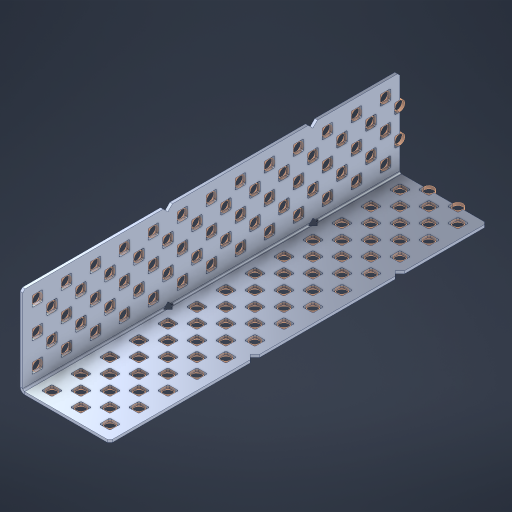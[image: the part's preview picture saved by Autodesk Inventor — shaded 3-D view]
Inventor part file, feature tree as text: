
AUTODESK INVENTOR PART (.ipt)
format: ipt  version: 2023 (Build 270158000, 158)  size: 1,572,352 bytes
history: native  units: in
note: dims shown in document units (in); Inventor stores cm internally (conversion verified against a paired STEP export)
features: other x136, extrude x128, sheet_metal_op x8, sketch x7, pattern_linear x3, mirror x1, chamfer x1
ambient origin geometry x8: Origin, YZ Plane, XZ Plane, XY Plane, X Axis, Y Axis, Z Axis, Center Point
bodies: Solid1 (feature_tree), Body (feature_tree)
feature tree (284):
  sheet_metal_op  "Flanges"
  sheet_metal_op  "Body Pattern"
  pattern_linear  "Center Double"  Spacing1=1.5in  [1 undecoded]
  pattern_linear  "Center Pattern"  Spacing1=0.1875in  [1 undecoded]
  other  "Arc Length"
  pattern_linear  "Notch Pattern"  Spacing1=0.0469in  [1 undecoded]
  other  "Diagonal Plane"
  mirror  "Everything Mirrored"
  chamfer  "End Chamfer"
  sketch  "Sketch1"  dims[d0=1.5in]
  other  "Plate1"
  sketch  "Sketch2"  dims[d1=6.5in]
  other  "Plate2"
  sheet_metal_op  "Bend1"
  sheet_metal_op  "Corner1"
  sketch  "Sketch8"  dims[d2=0.0469in]
  sketch  "Sketch9"  dims[d3=0.0469in]
  other  "Srf91"
  sheet_metal_op  "Body Pattern Sketch"
  other  "Srf92"
  sketch  "Sketch13"  dims[d4=0.0234in]
  sketch  "Sketch15"  dims[d5=0.0938in]
  sketch  "Sketch16"  dims[d6=0.0469in d7=1.5in d8=90.0deg d9=0.0312in d10=0.1875in d11=0.0469in d12=0.0469in d49=0.182in d50=0.02in d52=0.25in d53=0.0469in d54=0.0in d55=0.172in d56=1.0in d57=0.0in d85=0.1473in d86=0.1659in d89=0.0469in d90=0.0in d91=0.04in d92=0.0491in d95=2.5in d96=0.04in d97=0.25in d98=45.0deg d106=0.182in d107=0.02in d110=0.0469in d111=0.0in d112=0.172in d113=0.5in d114=0.0in d117=0.5in d126=0.0491in d127=0.1227in d128=0.08in d129=0.04in d130=2.5in d131=0.25in d132=5.1181in d134=0.5in d135=1.1811in d137=0.5in d140=0.5in d141=1.0in d142=0.3937in d144=0.5in d145=0.071in d146=0.7874in d148=0.5in]
  other  "Srf786"
  other  "Srf856"
  other  "Srf889"
  other  "Srf890"
  other  "Srf891"
  other  "Srf1275"
  other  "Srf1276"
  other  "Srf1278"
  other  "Srf1277"
  other  "Srf1285"
  other  "Srf1286"
  other  "Srf1287"
  other  "Srf1445"
  other  "Srf1446"
  other  "Srf1447"
  other  "Srf1448"
  other  "Srf1449"
  other  "Srf1537"
  other  "Srf1538"
  other  "Srf1539"
  other  "Srf1540"
  other  "Srf1541"
  other  "Srf1807"
  other  "Srf1808"
  other  "Srf1809"
  other  "Srf1810"
  other  "Srf1959"
  other  "Srf1960"
  other  "Srf1961"
  other  "Srf1962"
  other  "Srf2009"
  other  "Srf2010"
  other  "Srf2011"
  other  "Srf2012"
  other  "Srf2013"
  other  "Srf2014"
  other  "Srf2015"
  other  "Srf2016"
  other  "Srf2017"
  other  "Srf2018"
  other  "Srf2019"
  other  "Srf2020"
  other  "Srf2021"
  other  "Srf2043"
  other  "Srf2044"
  other  "Srf2045"
  other  "Srf2046"
  other  "Srf2047"
  other  "Srf2048"
  other  "Srf2049"
  other  "Srf2050"
  other  "Srf2051"
  other  "Srf2052"
  other  "Srf2053"
  other  "Srf2054"
  other  "Srf2076"
  other  "Srf2077"
  other  "Srf2078"
  other  "Srf2079"
  other  "Srf2080"
  other  "Srf2081"
  other  "Srf2082"
  other  "Srf2083"
  other  "Srf2084"
  other  "Srf2085"
  other  "Srf2086"
  other  "Srf2087"
  other  "Srf2088"
  other  "Srf2089"
  other  "Srf2090"
  other  "Srf2091"
  other  "Srf2092"
  other  "Srf2093"
  other  "Srf2094"
  other  "Srf2095"
  other  "Srf2096"
  other  "Srf2097"
  other  "Srf2098"
  other  "Srf2099"
  other  "Srf2100"
  other  "Srf2101"
  other  "Srf2102"
  other  "Srf2103"
  other  "Srf2104"
  other  "Srf2105"
  other  "Srf2106"
  other  "Srf2107"
  other  "Srf2108"
  other  "Srf2109"
  other  "Srf2110"
  other  "Srf2111"
  other  "Srf2112"
  other  "Srf2179"
  other  "Srf2180"
  other  "Srf2181"
  other  "Srf2182"
  other  "Srf2183"
  other  "Srf2184"
  other  "Srf2185"
  other  "Srf2186"
  other  "Srf2187"
  other  "Srf2188"
  other  "Srf2189"
  other  "Srf2190"
  other  "Srf2191"
  other  "Srf2192"
  other  "Srf2193"
  other  "Srf2194"
  other  "Srf2195"
  other  "Srf2196"
  other  "Srf2197"
  other  "Srf2198"
  other  "Srf2199"
  other  "Srf2200"
  other  "Srf2201"
  other  "Srf2202"
  other  "Srf2203"
  other  "Srf2204"
  other  "Srf2205"
  other  "Srf2206"
  other  "Srf2207"
  other  "Srf2208"
  other  "Srf2209"
  other  "Srf2210"
  other  "Srf2211"
  other  "Srf2212"
  other  "Srf2213"
  other  "Srf2214"
  sheet_metal_op  "Body Stamp"
  sheet_metal_op  "Body Circle"
  other  "Center Stamp"
  other  "Center Circle"
  sheet_metal_op  "Notch"
  extrude  "ExtrusionSrf92"  Depth=0.0469in
  extrude  "ExtrusionSrf856"  Depth=0.182in
  extrude  "ExtrusionSrf889"  Depth=0.02in
  extrude  "ExtrusionSrf890"  Depth=0.25in
  extrude  "ExtrusionSrf891"  Depth=0.0469in
  extrude  "ExtrusionSrf1275"  TaperAngle=0.0deg  [1 undecoded]
  extrude  "ExtrusionSrf1276"  Depth=0.5in
  extrude  "ExtrusionSrf1277"  Depth=1.0in TaperAngle=0.0deg
  extrude  "ExtrusionSrf1345"  Depth=0.5in
  extrude  "ExtrusionSrf1346"  Depth=0.5in
  extrude  "ExtrusionSrf1347"  Depth=0.0469in
  extrude  "ExtrusionSrf1348"  Depth=0.5in TaperAngle=0.0deg
  extrude  "ExtrusionSrf1445"  Depth=0.5in
  extrude  "ExtrusionSrf1446"  Depth=0.25in TaperAngle=45.0deg
  extrude  "ExtrusionSrf1447"  Depth=0.182in
  extrude  "ExtrusionSrf1448"  Depth=0.02in
  extrude  "ExtrusionSrf1449"  Depth=0.0469in
  extrude  "ExtrusionSrf1537"  TaperAngle=0.0deg  [1 undecoded]
  extrude  "ExtrusionSrf1538"  Depth=0.5in
  extrude  "ExtrusionSrf1539"  Depth=0.5in TaperAngle=0.0deg
  extrude  "ExtrusionSrf1540"  Depth=0.5in
  extrude  "ExtrusionSrf1541"  Depth=0.5in
  extrude  "ExtrusionSrf1807"  Depth=0.5in
  extrude  "ExtrusionSrf1808"  Depth=0.5in
  extrude  "ExtrusionSrf1809"  Depth=0.5in
  extrude  "ExtrusionSrf1810"  Depth=0.5in
  extrude  "ExtrusionSrf1959"  Depth=0.25in
  extrude  "ExtrusionSrf1960"  Depth=0.5in
  extrude  "ExtrusionSrf1961"  Depth=0.5in
  extrude  "ExtrusionSrf1962"  Depth=0.5in
  extrude  "ExtrusionSrf2009"  Depth=1.0in
  extrude  "ExtrusionSrf2010"  Depth=0.3937in
  extrude  "ExtrusionSrf2011"  Depth=0.5in
  extrude  "ExtrusionSrf2012"  Depth=0.5in
  extrude  "ExtrusionSrf2013"  [1 undecoded]
  extrude  "ExtrusionSrf2014"  [1 undecoded]
  extrude  "ExtrusionSrf2015"  [1 undecoded]
  extrude  "ExtrusionSrf2016"  [1 undecoded]
  extrude  "ExtrusionSrf2017"  [1 undecoded]
  extrude  "ExtrusionSrf2018"  [1 undecoded]
  extrude  "ExtrusionSrf2019"  [1 undecoded]
  extrude  "ExtrusionSrf2020"  [1 undecoded]
  extrude  "ExtrusionSrf2021"  [1 undecoded]
  extrude  "ExtrusionSrf2043"  [1 undecoded]
  extrude  "ExtrusionSrf2044"  [1 undecoded]
  extrude  "ExtrusionSrf2045"  [1 undecoded]
  extrude  "ExtrusionSrf2046"  [1 undecoded]
  extrude  "ExtrusionSrf2047"  [1 undecoded]
  extrude  "ExtrusionSrf2048"  [1 undecoded]
  extrude  "ExtrusionSrf2049"  [1 undecoded]
  extrude  "ExtrusionSrf2050"  [1 undecoded]
  extrude  "ExtrusionSrf2051"  [1 undecoded]
  extrude  "ExtrusionSrf2052"  [1 undecoded]
  extrude  "ExtrusionSrf2053"  [1 undecoded]
  extrude  "ExtrusionSrf2054"  [1 undecoded]
  extrude  "ExtrusionSrf2076"  [1 undecoded]
  extrude  "ExtrusionSrf2077"  [1 undecoded]
  extrude  "ExtrusionSrf2078"  [1 undecoded]
  extrude  "ExtrusionSrf2079"  [1 undecoded]
  extrude  "ExtrusionSrf2080"  [1 undecoded]
  extrude  "ExtrusionSrf2081"  [1 undecoded]
  extrude  "ExtrusionSrf2082"  [1 undecoded]
  extrude  "ExtrusionSrf2083"  [1 undecoded]
  extrude  "ExtrusionSrf2084"  [1 undecoded]
  extrude  "ExtrusionSrf2085"  [1 undecoded]
  extrude  "ExtrusionSrf2086"  [1 undecoded]
  extrude  "ExtrusionSrf2087"  [1 undecoded]
  extrude  "ExtrusionSrf2088"  [1 undecoded]
  extrude  "ExtrusionSrf2089"  [1 undecoded]
  extrude  "ExtrusionSrf2090"  [1 undecoded]
  extrude  "ExtrusionSrf2091"  [1 undecoded]
  extrude  "ExtrusionSrf2092"  [1 undecoded]
  extrude  "ExtrusionSrf2093"  [1 undecoded]
  extrude  "ExtrusionSrf2094"  [1 undecoded]
  extrude  "ExtrusionSrf2095"  [1 undecoded]
  extrude  "ExtrusionSrf2096"  [1 undecoded]
  extrude  "ExtrusionSrf2097"  [1 undecoded]
  extrude  "ExtrusionSrf2098"  [1 undecoded]
  extrude  "ExtrusionSrf2099"  [1 undecoded]
  extrude  "ExtrusionSrf2100"  [1 undecoded]
  extrude  "ExtrusionSrf2101"  [1 undecoded]
  extrude  "ExtrusionSrf2102"  [1 undecoded]
  extrude  "ExtrusionSrf2103"  [1 undecoded]
  extrude  "ExtrusionSrf2104"  [1 undecoded]
  extrude  "ExtrusionSrf2105"  [1 undecoded]
  extrude  "ExtrusionSrf2106"  [1 undecoded]
  extrude  "ExtrusionSrf2107"  [1 undecoded]
  extrude  "ExtrusionSrf2108"  [1 undecoded]
  extrude  "ExtrusionSrf2109"  [1 undecoded]
  extrude  "ExtrusionSrf2110"  [1 undecoded]
  extrude  "ExtrusionSrf2111"  [1 undecoded]
  extrude  "ExtrusionSrf2112"  [1 undecoded]
  extrude  "ExtrusionSrf2179"  [1 undecoded]
  extrude  "ExtrusionSrf2180"  [1 undecoded]
  extrude  "ExtrusionSrf2181"  [1 undecoded]
  extrude  "ExtrusionSrf2182"  [1 undecoded]
  extrude  "ExtrusionSrf2183"  [1 undecoded]
  extrude  "ExtrusionSrf2184"  [1 undecoded]
  extrude  "ExtrusionSrf2185"  [1 undecoded]
  extrude  "ExtrusionSrf2186"  [1 undecoded]
  extrude  "ExtrusionSrf2187"  [1 undecoded]
  extrude  "ExtrusionSrf2188"  [1 undecoded]
  extrude  "ExtrusionSrf2189"  [1 undecoded]
  extrude  "ExtrusionSrf2190"  [1 undecoded]
  extrude  "ExtrusionSrf2191"  [1 undecoded]
  extrude  "ExtrusionSrf2192"  [1 undecoded]
  extrude  "ExtrusionSrf2193"  [1 undecoded]
  extrude  "ExtrusionSrf2194"  [1 undecoded]
  extrude  "ExtrusionSrf2195"  [1 undecoded]
  extrude  "ExtrusionSrf2196"  [1 undecoded]
  extrude  "ExtrusionSrf2197"  [1 undecoded]
  extrude  "ExtrusionSrf2198"  [1 undecoded]
  extrude  "ExtrusionSrf2199"  [1 undecoded]
  extrude  "ExtrusionSrf2200"  [1 undecoded]
  extrude  "ExtrusionSrf2201"  [1 undecoded]
  extrude  "ExtrusionSrf2202"  [1 undecoded]
  extrude  "ExtrusionSrf2203"  [1 undecoded]
  extrude  "ExtrusionSrf2204"  [1 undecoded]
  extrude  "ExtrusionSrf2205"  [1 undecoded]
  extrude  "ExtrusionSrf2206"  [1 undecoded]
  extrude  "ExtrusionSrf2207"  [1 undecoded]
  extrude  "ExtrusionSrf2208"  [1 undecoded]
  extrude  "ExtrusionSrf2209"  [1 undecoded]
  extrude  "ExtrusionSrf2210"  [1 undecoded]
  extrude  "ExtrusionSrf2211"  [1 undecoded]
  extrude  "ExtrusionSrf2212"  [1 undecoded]
  extrude  "ExtrusionSrf2213"  [1 undecoded]
  extrude  "ExtrusionSrf2214"  [1 undecoded]
note: 99 required parameter values undecoded (feature->parameter linkage not recoverable at this tier; creation-order binding heuristic only, values carry confidence <= 0.55)
